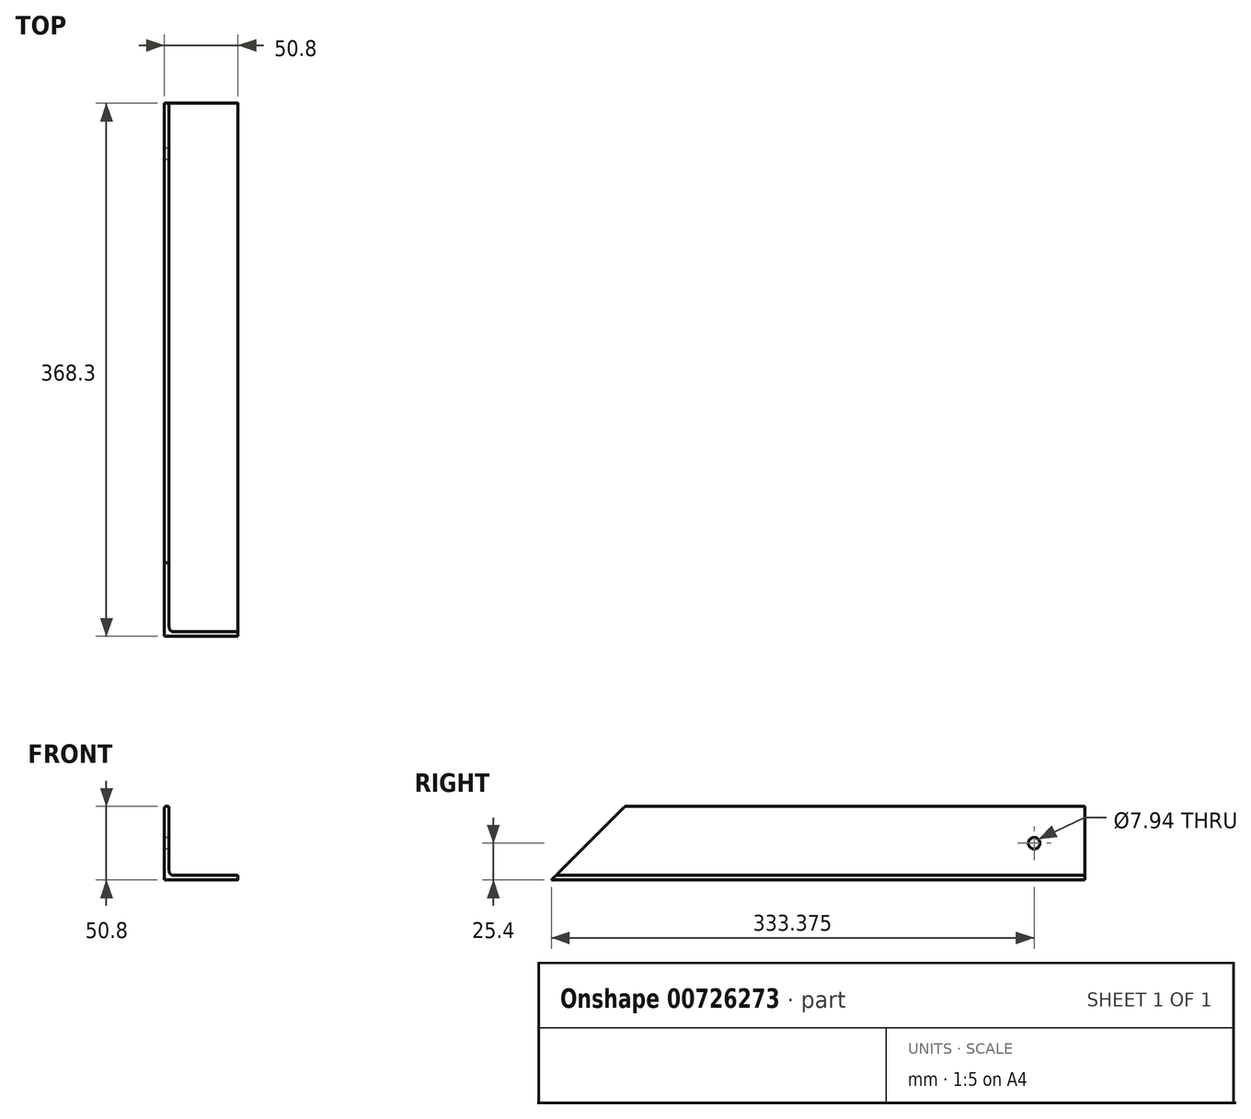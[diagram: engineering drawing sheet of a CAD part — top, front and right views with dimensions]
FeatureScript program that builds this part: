
annotation { "Feature Type Name" : "Feature", "Feature Type Description" : "" }
export const myFeature = defineFeature(function(context is Context, id is Id, definition is map)
    precondition{}
    {
        {
            var Q0;
            Q0=qCreatedBy(makeId("Front.planeOp"),FACE);
            var sketch = newSketch(context, id + "F0", { "sketchPlane" : qUnion([Q0])});
            skLineSegment(sketch, "E0.bottom", {"start": v(0, 0) * mm, "end": v(50.04, 0) * mm});
            skLineSegment(sketch, "E0.top", {"start": v(0.76, 50.8) * mm, "end": v(2.41, 50.8) * mm});
            skLineSegment(sketch, "E0.left", {"start": v(0, 0) * mm, "end": v(0, 50.04) * mm});
            skLineSegment(sketch, "E0.right", {"start": v(50.8, 0.76) * mm, "end": v(50.8, 2.41) * mm});
            skLineSegment(sketch, "E1", {"start": v(3.17, 50.04) * mm, "end": v(3.17, 6.35) * mm});
            skLineSegment(sketch, "E2", {"start": v(6.35, 3.17) * mm, "end": v(50.04, 3.18) * mm});
            skPoint(sketch, "E3.visualSharp", {"position": v(3.17, 3.17) * mm});
            skArc(sketch, "E3.filletArc", {"start": v(3.17, 6.35) * mm, "mid": v(4.1, 4.1) * mm, "end": v(6.35, 3.17) * mm});
            skPoint(sketch, "E4.visualSharp", {"position": v(50.8, 0) * mm});
            skArc(sketch, "E4.filletArc", {"start": v(50.04, 0) * mm, "mid": v(50.58, 0.22) * mm, "end": v(50.8, 0.76) * mm});
            skPoint(sketch, "E5.visualSharp", {"position": v(3.17, 50.8) * mm});
            skArc(sketch, "E5.filletArc", {"start": v(3.17, 50.04) * mm, "mid": v(2.95, 50.58) * mm, "end": v(2.41, 50.8) * mm});
            skPoint(sketch, "E6.visualSharp", {"position": v(0, 50.8) * mm});
            skArc(sketch, "E6.filletArc", {"start": v(0.76, 50.8) * mm, "mid": v(0.22, 50.58) * mm, "end": v(0, 50.04) * mm});
            skPoint(sketch, "E7.visualSharp", {"position": v(50.8, 3.18) * mm});
            skArc(sketch, "E7.filletArc", {"start": v(50.8, 2.41) * mm, "mid": v(50.58, 2.95) * mm, "end": v(50.04, 3.18) * mm});
            skSolve(sketch);
        }
        {
            var Q0;
            Q0 = qSketchRegion(id + "F0", true);
            extrude(context, id + "F1", {"entities" : qUnion([Q0]), "depth" : 368.3 * mm, "offsetDistance" : 25.4 * mm});
        }
        {
            var Q0;
            Q0=makeQuery(id+"F1.opExtrude","SWEPT_FACE",FACE,{"disambiguationData":[OSD([sQuery(id+"F0.wireOp",EDGE,"E0.left")])]});
            var sketch = newSketch(context, id + "F2", { "sketchPlane" : qUnion([Q0])});
            skLineSegment(sketch, "E8", {"start": v(368.3, 6.35) * mm, "end": v(368.3, 6.35) * mm});
            skLineSegment(sketch, "E9", {"start": v(368.3, 0) * mm, "end": v(310.94, 57.36) * mm});
            skLineSegment(sketch, "E10", {"start": v(310.94, 57.36) * mm, "end": v(368.3, 57.36) * mm});
            skLineSegment(sketch, "E11", {"start": v(368.3, 57.36) * mm, "end": v(368.3, 0) * mm});
            skSolve(sketch);
        }
        {
            var Q0;
            {var subQ0=sQuery(id+"F2.wireOp",EDGE,"E10");Q0=makeQuery(id+"F2.imprint","IMPRINT",FACE,{"disambiguationData":[TD([[makeQuery(id+"F2.imprint","IMPRINT",EDGE,{"derivedFrom":subQ0}),-1.0]])]});}
            var Q1;
            {var subQ1=sQuery(id+"F2.wireOp",EDGE,"E9");var subQ2=sQuery(id+"F0.wireOp",EDGE,"E0.left");var subQ4=makeQuery(id+"F1.opExtrude","SWEPT_EDGE",EDGE,{"disambiguationData":[OSD([subQ2,sQuery(id+"F0.wireOp",EDGE,"E6.filletArc")])]});var subQ5=makeQuery(id+"F2.imprint","INTERSECT",VERTEX,{"derivedFrom":[subQ4,subQ1]});Q1=makeQuery(id+"F2.imprint","IMPRINT",FACE,{"disambiguationData":[TD([[makeQuery(id+"F2.imprint","IMPRINT",EDGE,{"disambiguationData":[TD([[subQ5,1.0]])],"derivedFrom":subQ1}),-1.0]])]});}
            extrude(context, id + "F3", {"entities" : qUnion([Q0, Q1]), "operationType" : NewBodyOperationType.REMOVE, "endBound" : BoundingType.THROUGH_ALL, "oppositeDirection" : true, "depth" : 25.4 * mm, "offsetDistance" : 25.4 * mm});
        }
        {
            var Q0;
            Q0=makeQuery(id+"F1.opExtrude","SWEPT_FACE",FACE,{"disambiguationData":[OSD([sQuery(id+"F0.wireOp",EDGE,"E0.left")])]});
            var sketch = newSketch(context, id + "F4", { "sketchPlane" : qUnion([Q0])});
            skCircle(sketch, "E12", {"center": v(34.93, 25.4) * mm, "radius": 3.97 * mm});
            skSolve(sketch);
        }
        {
            var Q0;
            Q0 = qSketchRegion(id + "F4", true);
            extrude(context, id + "F5", {"entities" : qUnion([Q0]), "operationType" : NewBodyOperationType.REMOVE, "endBound" : BoundingType.THROUGH_ALL, "oppositeDirection" : true, "depth" : 25.4 * mm, "offsetDistance" : 25.4 * mm});
        }
    });
